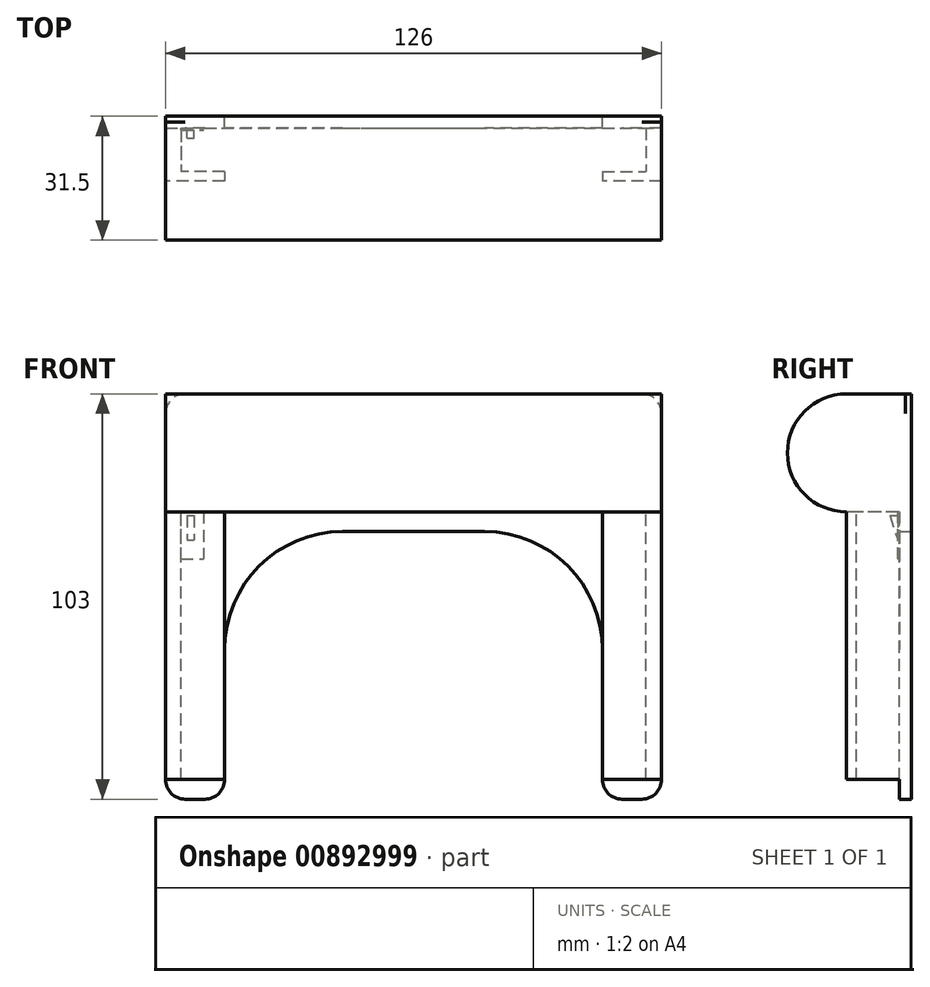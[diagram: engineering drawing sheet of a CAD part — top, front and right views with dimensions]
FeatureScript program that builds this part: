
annotation { "Feature Type Name" : "Feature", "Feature Type Description" : "" }
export const myFeature = defineFeature(function(context is Context, id is Id, definition is map)
    precondition{}
    {
        {
            var Q0;
            Q0=qCreatedBy(makeId("Front.planeOp"),FACE);
            var sketch = newSketch(context, id + "F0", { "sketchPlane" : qUnion([Q0])});
            skLineSegment(sketch, "E0.bottom", {"start": v(58, -51.5) * mm, "end": v(53, -51.5) * mm});
            skLineSegment(sketch, "E0.top", {"start": v(58, 51.5) * mm, "end": v(-58, 51.5) * mm});
            skLineSegment(sketch, "E0.left", {"start": v(63, -46.5) * mm, "end": v(63, 46.5) * mm});
            skLineSegment(sketch, "E0.right", {"start": v(-63, -46.5) * mm, "end": v(-63, 46.5) * mm});
            skPoint(sketch, "E0.middle", {"position": v(0, 0) * mm});
            skLineSegment(sketch, "E1.top", {"start": v(-18, 16.5) * mm, "end": v(18, 16.5) * mm});
            skLineSegment(sketch, "E1.left", {"start": v(-48, -46.5) * mm, "end": v(-48, -13.5) * mm});
            skLineSegment(sketch, "E1.right", {"start": v(48, -46.5) * mm, "end": v(48, -13.5) * mm});
            skLineSegment(sketch, "E2.trimOffspring", {"start": v(-53, -51.5) * mm, "end": v(-58, -51.5) * mm});
            skPoint(sketch, "E3.visualSharp", {"position": v(-63, 51.5) * mm});
            skArc(sketch, "E3.filletArc", {"start": v(-58, 51.5) * mm, "mid": v(-61.54, 50.04) * mm, "end": v(-63, 46.5) * mm});
            skPoint(sketch, "E4.visualSharp", {"position": v(-63, -51.5) * mm});
            skArc(sketch, "E4.filletArc", {"start": v(-63, -46.5) * mm, "mid": v(-61.54, -50.04) * mm, "end": v(-58, -51.5) * mm});
            skPoint(sketch, "E5.visualSharp", {"position": v(-48, -51.5) * mm});
            skArc(sketch, "E5.filletArc", {"start": v(-53, -51.5) * mm, "mid": v(-49.46, -50.04) * mm, "end": v(-48, -46.5) * mm});
            skPoint(sketch, "E6.visualSharp", {"position": v(48, -51.5) * mm});
            skArc(sketch, "E6.filletArc", {"start": v(48, -46.5) * mm, "mid": v(49.46, -50.04) * mm, "end": v(53, -51.5) * mm});
            skPoint(sketch, "E7.visualSharp", {"position": v(63, -51.5) * mm});
            skArc(sketch, "E7.filletArc", {"start": v(58, -51.5) * mm, "mid": v(61.54, -50.04) * mm, "end": v(63, -46.5) * mm});
            skPoint(sketch, "E8.visualSharp", {"position": v(63, 51.5) * mm});
            skArc(sketch, "E8.filletArc", {"start": v(63, 46.5) * mm, "mid": v(61.54, 50.04) * mm, "end": v(58, 51.5) * mm});
            skPoint(sketch, "E9.visualSharp", {"position": v(-48, 16.5) * mm});
            skArc(sketch, "E9.filletArc", {"start": v(-18, 16.5) * mm, "mid": v(-39.21, 7.71) * mm, "end": v(-48, -13.5) * mm});
            skPoint(sketch, "E10.visualSharp", {"position": v(48, 16.5) * mm});
            skArc(sketch, "E10.filletArc", {"start": v(48, -13.5) * mm, "mid": v(39.21, 7.71) * mm, "end": v(18, 16.5) * mm});
            skSolve(sketch);
        }
        {
            var Q0;
            Q0=makeQuery(id+"F0.imprint","IMPRINT",FACE,{"disambiguationData":[TD([[makeQuery(id+"F0.imprint","IMPRINT",EDGE,{"derivedFrom":sQuery(id+"F0.wireOp",EDGE,"E0.bottom")}),-1.0]])]});
            extrude(context, id + "F1", {"entities" : qUnion([Q0]), "endBound" : BoundingType.SYMMETRIC, "depth" : 3 * mm, "offsetDistance" : 25 * mm});
        }
        {
            var Q0;
            Q0=qCreatedBy(makeId("Right.planeOp"),FACE);
            var sketch = newSketch(context, id + "F2", { "sketchPlane" : qUnion([Q0])});
            skLineSegment(sketch, "E11.bottom", {"start": v(0, 51.5) * mm, "end": v(-15, 51.5) * mm});
            skLineSegment(sketch, "E11.top", {"start": v(0, 21.5) * mm, "end": v(-15, 21.5) * mm});
            skLineSegment(sketch, "E11.left", {"start": v(0, 51.5) * mm, "end": v(0, 21.5) * mm});
            skLineSegment(sketch, "E11.right", {"start": v(-30, 36.5) * mm, "end": v(-30, 36.5) * mm});
            skPoint(sketch, "E12.visualSharp", {"position": v(-30, 51.5) * mm});
            skArc(sketch, "E12.filletArc", {"start": v(-15, 51.5) * mm, "mid": v(-25.6, 47.1) * mm, "end": v(-30, 36.5) * mm});
            skPoint(sketch, "E13.visualSharp", {"position": v(-30, 21.5) * mm});
            skArc(sketch, "E13.filletArc", {"start": v(-30, 36.5) * mm, "mid": v(-25.6, 25.9) * mm, "end": v(-15, 21.5) * mm});
            skSolve(sketch);
        }
        {
            var Q0;
            Q0=makeQuery(id+"F2.imprint","IMPRINT",FACE,{"disambiguationData":[TD([[makeQuery(id+"F2.imprint","IMPRINT",EDGE,{"derivedFrom":sQuery(id+"F2.wireOp",EDGE,"E11.bottom")}),1.0]])]});
            extrude(context, id + "F3", {"entities" : qUnion([Q0]), "operationType" : NewBodyOperationType.ADD, "endBound" : BoundingType.SYMMETRIC, "depth" : 126 * mm, "offsetDistance" : 25 * mm});
        }
        {
            var Q0;
            Q0=makeQuery(id+"F3.opExtrude","SWEPT_FACE",FACE,{"disambiguationData":[OSD([sQuery(id+"F2.wireOp",EDGE,"E11.top")])]});
            var sketch = newSketch(context, id + "F4", { "sketchPlane" : qUnion([Q0])});
            skLineSegment(sketch, "E14.bottom", {"start": v(-63, 1.5) * mm, "end": v(-59, 1.5) * mm});
            skLineSegment(sketch, "E14.top", {"start": v(-63, 15) * mm, "end": v(-48, 15) * mm});
            skLineSegment(sketch, "E14.left", {"start": v(-63, 1.5) * mm, "end": v(-63, 15) * mm});
            skLineSegment(sketch, "E14.right", {"start": v(-48, 12.5) * mm, "end": v(-48, 15) * mm});
            skLineSegment(sketch, "E15.top", {"start": v(-48, 12.5) * mm, "end": v(-59, 12.5) * mm});
            skLineSegment(sketch, "E15.right", {"start": v(-59, 1.5) * mm, "end": v(-59, 12.5) * mm});
            skSolve(sketch);
        }
        {
            var Q0;
            Q0=makeQuery(id+"F4.imprint","IMPRINT",FACE,{"disambiguationData":[TD([[makeQuery(id+"F4.imprint","IMPRINT",EDGE,{"derivedFrom":sQuery(id+"F4.wireOp",EDGE,"E14.bottom")}),1.0]])]});
            var sketch = newSketch(context, id + "F5", { "sketchPlane" : qUnion([Q0])});
            skSolve(sketch);
        }
        {
            var Q0;
            Q0=makeQuery(id+"F5.imprint","IMPRINT",FACE,{"disambiguationData":[TD([[makeQuery(id+"F5.imprint","IMPRINT",EDGE,{"derivedFrom":makeQuery(id+"F4.imprint","IMPRINT",EDGE,{"derivedFrom":sQuery(id+"F4.wireOp",EDGE,"E14.bottom")})}),1.0]])]});
            extrude(context, id + "F6", {"entities" : qUnion([Q0]), "operationType" : NewBodyOperationType.ADD, "depth" : 68 * mm, "offsetDistance" : 25 * mm});
        }
        {
            var Q0;
            Q0=makeQuery(id+"F1.opExtrude","SWEPT_BODY",BODY,{"disambiguationData":[OSD([sQuery(id+"F0.wireOp",EDGE,"E0.bottom"),sQuery(id+"F0.wireOp",EDGE,"E0.top"),sQuery(id+"F0.wireOp",EDGE,"E0.left"),sQuery(id+"F0.wireOp",EDGE,"E0.right"),sQuery(id+"F0.wireOp",EDGE,"E1.top"),sQuery(id+"F0.wireOp",EDGE,"E1.left"),sQuery(id+"F0.wireOp",EDGE,"E1.right"),sQuery(id+"F0.wireOp",EDGE,"E2.trimOffspring"),sQuery(id+"F0.wireOp",EDGE,"E3.filletArc"),sQuery(id+"F0.wireOp",EDGE,"E4.filletArc"),sQuery(id+"F0.wireOp",EDGE,"E5.filletArc"),sQuery(id+"F0.wireOp",EDGE,"E6.filletArc"),sQuery(id+"F0.wireOp",EDGE,"E7.filletArc"),sQuery(id+"F0.wireOp",EDGE,"E8.filletArc"),sQuery(id+"F0.wireOp",EDGE,"E9.filletArc"),sQuery(id+"F0.wireOp",EDGE,"E10.filletArc")])]});
            var Q1;
            Q1=qCreatedBy(makeId("Right.planeOp"),FACE);
            mirror(context, id + "F7", {"operationType" : NewBodyOperationType.ADD, "entities" : qUnion([Q0]), "mirrorPlane" : qUnion([Q1])});
        }
        {
            var Q0;
            Q0=makeQuery(id+"F1.opExtrude","CAP_FACE",FACE,{"disambiguationData":[OSD([sQuery(id+"F0.wireOp",EDGE,"E0.bottom"),sQuery(id+"F0.wireOp",EDGE,"E0.top"),sQuery(id+"F0.wireOp",EDGE,"E0.left"),sQuery(id+"F0.wireOp",EDGE,"E0.right"),sQuery(id+"F0.wireOp",EDGE,"E1.top"),sQuery(id+"F0.wireOp",EDGE,"E1.left"),sQuery(id+"F0.wireOp",EDGE,"E1.right"),sQuery(id+"F0.wireOp",EDGE,"E2.trimOffspring"),sQuery(id+"F0.wireOp",EDGE,"E3.filletArc"),sQuery(id+"F0.wireOp",EDGE,"E4.filletArc"),sQuery(id+"F0.wireOp",EDGE,"E5.filletArc"),sQuery(id+"F0.wireOp",EDGE,"E6.filletArc"),sQuery(id+"F0.wireOp",EDGE,"E7.filletArc"),sQuery(id+"F0.wireOp",EDGE,"E8.filletArc"),sQuery(id+"F0.wireOp",EDGE,"E9.filletArc"),sQuery(id+"F0.wireOp",EDGE,"E10.filletArc")])],"isStart":false});
            var sketch = newSketch(context, id + "F8", { "sketchPlane" : qUnion([Q0])});
            skLineSegment(sketch, "E16.bottom", {"start": v(-59, 21.5) * mm, "end": v(-53.34, 21.5) * mm});
            skLineSegment(sketch, "E16.top", {"start": v(-59, 9.5) * mm, "end": v(-53.34, 9.5) * mm});
            skLineSegment(sketch, "E16.left", {"start": v(-59, 21.5) * mm, "end": v(-59, 9.5) * mm});
            skLineSegment(sketch, "E16.right", {"start": v(-53.34, 21.5) * mm, "end": v(-53.34, 9.5) * mm});
            skSolve(sketch);
        }
        {
            var Q0;
            Q0 = qSketchRegion(id + "F8", true);
            extrude(context, id + "F9", {"entities" : qUnion([Q0]), "operationType" : NewBodyOperationType.ADD, "depth" : 0.5 * mm, "offsetDistance" : 25 * mm});
        }
        {
            var Q0;
            Q0=makeQuery(id+"F9.opExtrude","CAP_FACE",FACE,{"disambiguationData":[OSD([sQuery(id+"F8.wireOp",EDGE,"E16.bottom"),sQuery(id+"F8.wireOp",EDGE,"E16.top"),sQuery(id+"F8.wireOp",EDGE,"E16.left"),sQuery(id+"F8.wireOp",EDGE,"E16.right")])],"isStart":false});
            var sketch = newSketch(context, id + "F10", { "sketchPlane" : qUnion([Q0])});
            skLineSegment(sketch, "E17.bottom", {"start": v(-57.48, 20.55) * mm, "end": v(-55.78, 20.55) * mm});
            skLineSegment(sketch, "E17.top", {"start": v(-57.48, 14.3) * mm, "end": v(-55.78, 14.3) * mm});
            skLineSegment(sketch, "E17.left", {"start": v(-57.48, 20.55) * mm, "end": v(-57.48, 14.3) * mm});
            skLineSegment(sketch, "E17.right", {"start": v(-55.78, 20.55) * mm, "end": v(-55.78, 14.3) * mm});
            skSolve(sketch);
        }
        {
            var Q0;
            Q0 = qSketchRegion(id + "F10", true);
            extrude(context, id + "F11", {"entities" : qUnion([Q0]), "operationType" : NewBodyOperationType.ADD, "depth" : 2 * mm, "offsetDistance" : 25 * mm});
        }
        {
            var Q0;
            Q0=makeQuery(id+"F11.opExtrude","SWEPT_FACE",FACE,{"disambiguationData":[OSD([sQuery(id+"F10.wireOp",EDGE,"E17.right")])]});
            var sketch = newSketch(context, id + "F12", { "sketchPlane" : qUnion([Q0])});
            skLineSegment(sketch, "E18", {"start": v(-4, 20.55) * mm, "end": v(-2, 14.3) * mm});
            skLineSegment(sketch, "E19", {"start": v(-4, 14.3) * mm, "end": v(-2, 14.3) * mm});
            skLineSegment(sketch, "E20", {"start": v(-4, 14.3) * mm, "end": v(-4, 20.55) * mm});
            skSolve(sketch);
        }
        {
            var Q0;
            Q0=makeQuery(id+"F12.imprint","IMPRINT",FACE,{"disambiguationData":[TD([[makeQuery(id+"F12.imprint","IMPRINT",EDGE,{"derivedFrom":sQuery(id+"F12.wireOp",EDGE,"E18")}),-1.0]])]});
            extrude(context, id + "F13", {"entities" : qUnion([Q0]), "operationType" : NewBodyOperationType.REMOVE, "oppositeDirection" : true, "depth" : 3 * mm, "offsetDistance" : 25 * mm});
        }
    });
